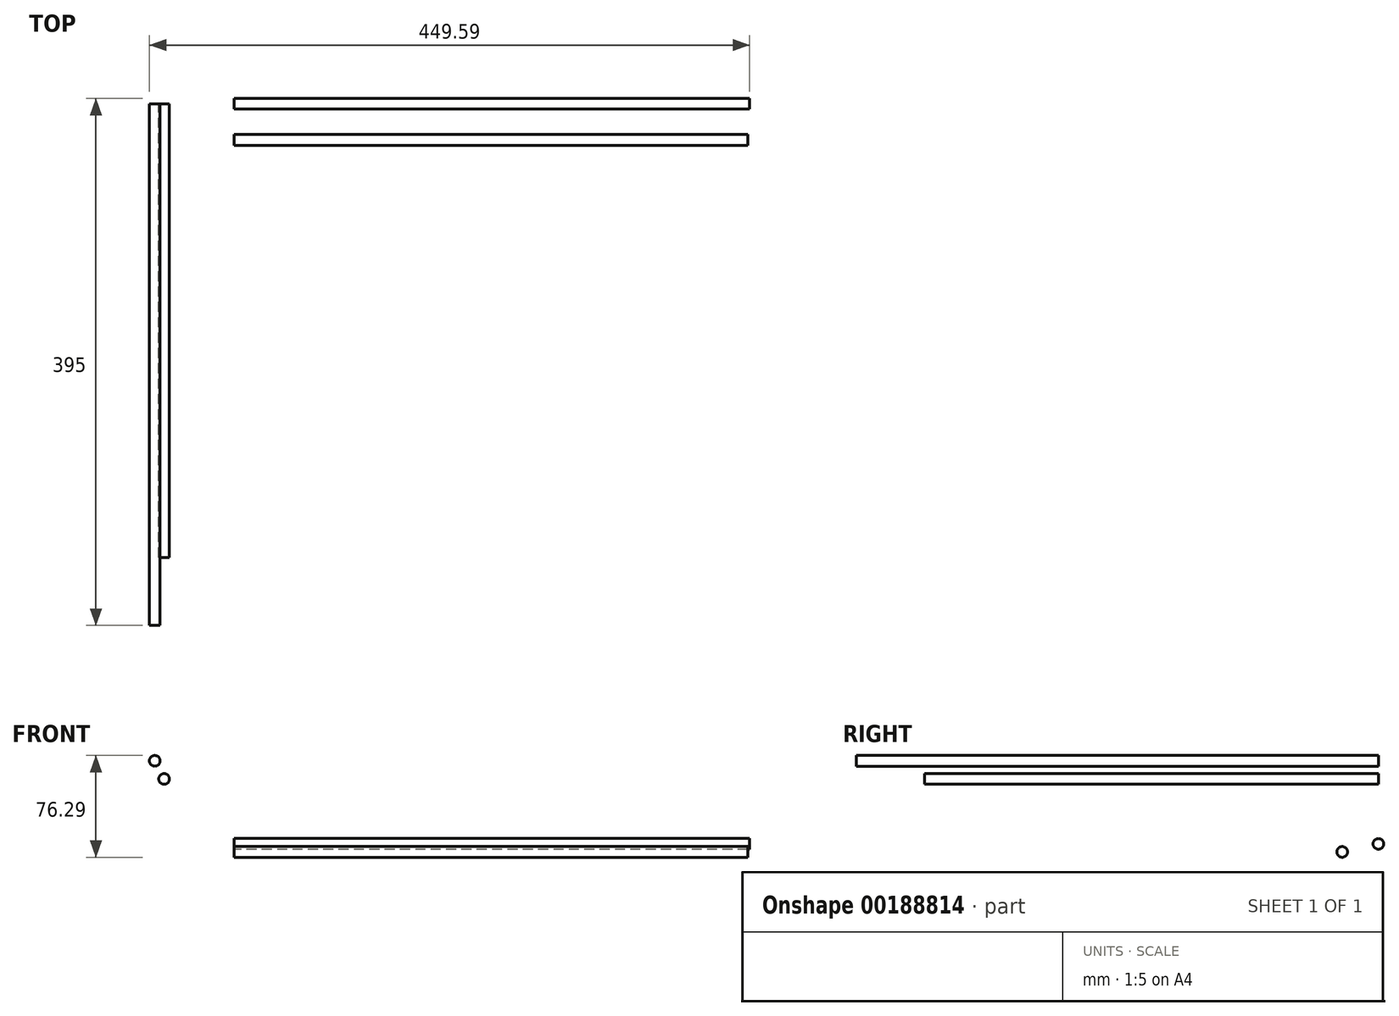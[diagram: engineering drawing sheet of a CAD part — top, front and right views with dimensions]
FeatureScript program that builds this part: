
annotation { "Feature Type Name" : "Feature", "Feature Type Description" : "" }
export const myFeature = defineFeature(function(context is Context, id is Id, definition is map)
    precondition{}
    {
        {
            assignVariable(context, id + "F0", {"name" : "X", "anyValue" : 299});
        }
        {
            assignVariable(context, id + "F1", {"name" : "Y", "anyValue" : 308});
        }
        {
            var Q0;
            Q0=qCreatedBy(makeId("Right.planeOp"),FACE);
            var sketch = newSketch(context, id + "F2", { "sketchPlane" : qUnion([Q0])});
            skCircle(sketch, "E0", {"center": v(0, 0) * mm, "radius": 4 * mm});
            skSolve(sketch);
        }
        {
            var Q0;
            Q0=qCreatedBy(makeId("Front.planeOp"),FACE);
            var sketch = newSketch(context, id + "F3", { "sketchPlane" : qUnion([Q0])});
            skCircle(sketch, "E1", {"center": v(-59.4, 62.27) * mm, "radius": 4 * mm});
            skSolve(sketch);
        }
        {
            var Q0;
            Q0=qCreatedBy(makeId("Right.planeOp"),FACE);
            var sketch = newSketch(context, id + "F4", { "sketchPlane" : qUnion([Q0])});
            skCircle(sketch, "E2", {"center": v(-27.06, -6.02) * mm, "radius": 4 * mm});
            skSolve(sketch);
        }
        {
            var Q0;
            Q0=makeQuery(id+"F2.imprint","IMPRINT",FACE,{"disambiguationData":[TD([[makeQuery(id+"F2.imprint","IMPRINT",EDGE,{"derivedFrom":sQuery(id+"F2.wireOp",EDGE,"E0")}),1.0]])]});
            var Q1;
            Q1=sQuery(id+"F2.wireOp",EDGE,"E0");
            extrude(context, id + "F5", {"entities" : qUnion([Q0]), "surfaceEntities" : qUnion([Q1]), "depth" : (getVariable(context, 'X') + 87.17) * mm});
        }
        {
            var Q0;
            Q0=makeQuery(id+"F3.imprint","IMPRINT",FACE,{"disambiguationData":[TD([[makeQuery(id+"F3.imprint","IMPRINT",EDGE,{"derivedFrom":sQuery(id+"F3.wireOp",EDGE,"E1")}),1.0]])]});
            var Q1;
            Q1=sQuery(id+"F3.wireOp",EDGE,"E1");
            extrude(context, id + "F6", {"entities" : qUnion([Q0]), "surfaceEntities" : qUnion([Q1]), "depth" : (getVariable(context, 'Y') + 83) * mm});
        }
        {
            var Q0;
            Q0=qCreatedBy(makeId("Front.planeOp"),FACE);
            var sketch = newSketch(context, id + "F7", { "sketchPlane" : qUnion([Q0])});
            skCircle(sketch, "E3", {"center": v(-52.4, 48.69) * mm, "radius": 4 * mm});
            skSolve(sketch);
        }
        {
            var Q0;
            Q0=makeQuery(id+"F7.imprint","IMPRINT",FACE,{"disambiguationData":[TD([[makeQuery(id+"F7.imprint","IMPRINT",EDGE,{"derivedFrom":sQuery(id+"F7.wireOp",EDGE,"E3")}),1.0]])]});
            extrude(context, id + "F8", {"entities" : qUnion([Q0]), "depth" : 340 * mm});
        }
        {
            var Q0;
            Q0=makeQuery(id+"F4.imprint","IMPRINT",FACE,{"disambiguationData":[TD([[makeQuery(id+"F4.imprint","IMPRINT",EDGE,{"derivedFrom":sQuery(id+"F4.wireOp",EDGE,"E2")}),1.0]])]});
            var Q1;
            Q1=sQuery(id+"F4.wireOp",EDGE,"E2");
            extrude(context, id + "F9", {"entities" : qUnion([Q0]), "surfaceEntities" : qUnion([Q1]), "depth" : (386 - 1.2) * mm});
        }
    });
